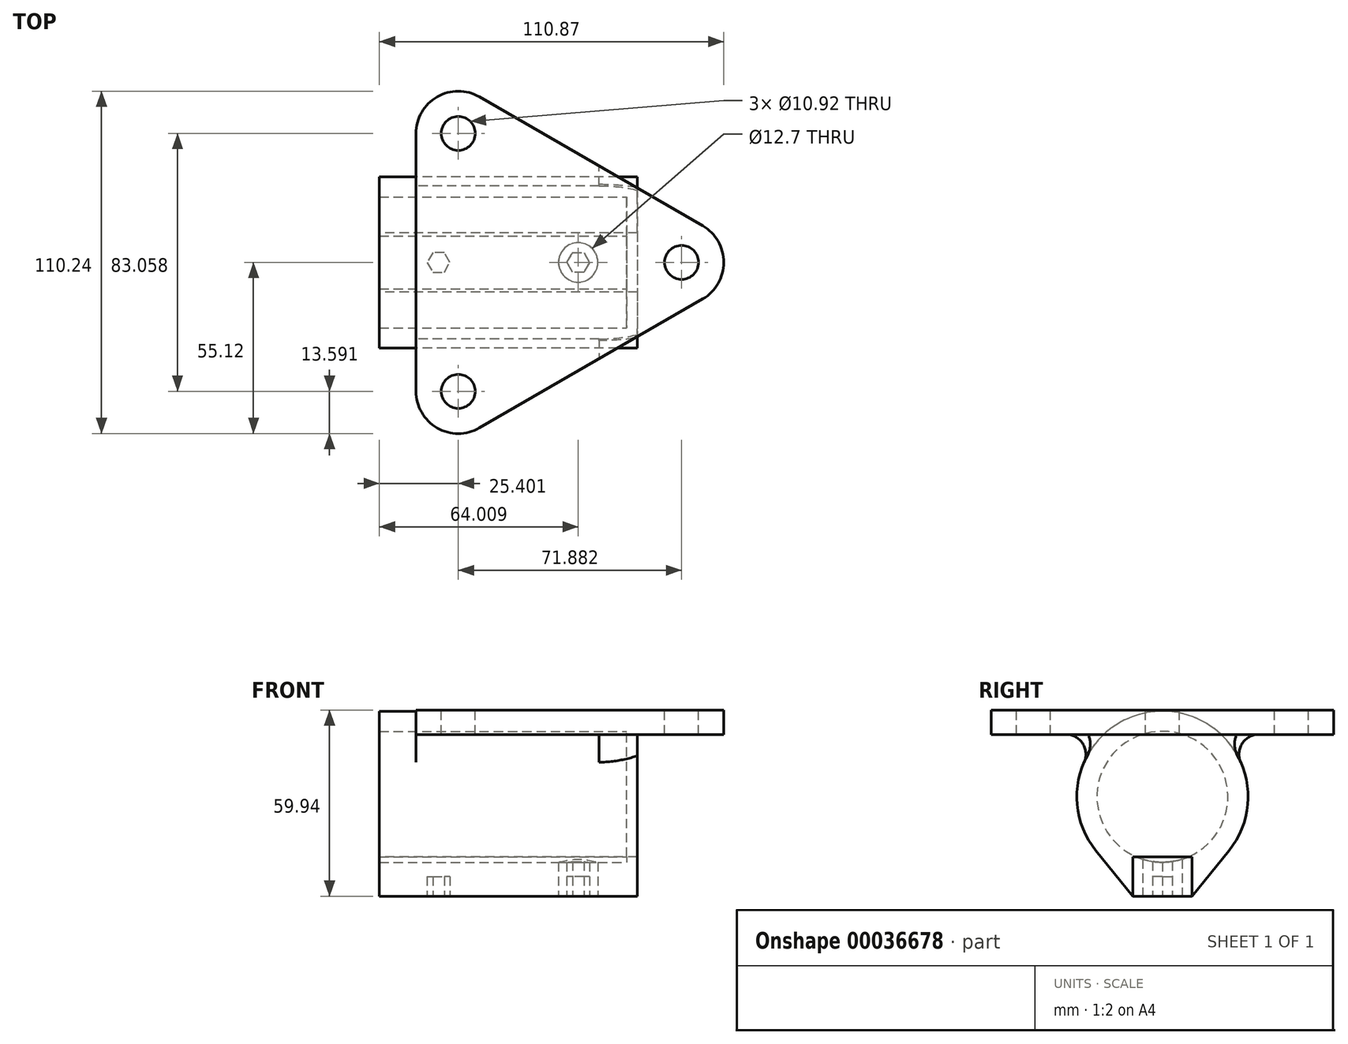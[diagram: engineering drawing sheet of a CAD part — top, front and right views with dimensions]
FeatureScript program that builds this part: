
annotation { "Feature Type Name" : "Feature", "Feature Type Description" : "" }
export const myFeature = defineFeature(function(context is Context, id is Id, definition is map)
    precondition{}
    {
        {
            var Q0;
            Q0=qCreatedBy(makeId("Right.planeOp"),FACE);
            var sketch = newSketch(context, id + "F0", { "sketchPlane" : qUnion([Q0])});
            skCircle(sketch, "E0", {"center": v(0, 0) * mm, "radius": 21.08 * mm});
            skCircle(sketch, "E1", {"center": v(0, 0) * mm, "radius": 27.56 * mm});
            skLineSegment(sketch, "E2.rect.top", {"start": v(9.53, -32) * mm, "end": v(-9.53, -32) * mm});
            skLineSegment(sketch, "E3", {"start": v(-9.52, -32) * mm, "end": v(-21.4, -17.36) * mm});
            skLineSegment(sketch, "E4", {"start": v(9.53, -32) * mm, "end": v(21.4, -17.36) * mm});
            skSolve(sketch);
        }
        {
            var Q0;
            Q0=makeQuery(id+"F0.imprint","IMPRINT",FACE,{"disambiguationData":[TD([[makeQuery(id+"F0.imprint","IMPRINT",EDGE,{"derivedFrom":sQuery(id+"F0.wireOp",EDGE,"E0")}),-1.0]])]});
            var Q1;
            Q1=makeQuery(id+"F0.imprint","IMPRINT",FACE,{"disambiguationData":[TD([[makeQuery(id+"F0.imprint","IMPRINT",EDGE,{"derivedFrom":sQuery(id+"F0.wireOp",EDGE,"E2.rect.top")}),-1.0]])]});
            var Q2;
            Q2=makeQuery(id+"F0.imprint","IMPRINT",FACE,{"disambiguationData":[TD([[makeQuery(id+"F0.imprint","IMPRINT",EDGE,{"derivedFrom":sQuery(id+"F0.wireOp",EDGE,"E0")}),1.0]])]});
            extrude(context, id + "F1", {"entities" : qUnion([Q0, Q1, Q2]), "endBound" : BoundingType.SYMMETRIC, "depth" : 83.06 * mm});
        }
        {
            var Q0;
            Q0=makeQuery(id+"F1.opExtrude","SWEPT_FACE",FACE,{"disambiguationData":[OSD([sQuery(id+"F0.wireOp",EDGE,"E2.rect.top")])]});
            var sketch = newSketch(context, id + "F2", { "sketchPlane" : qUnion([Q0])});
            skCircle(sketch, "E5", {"center": v(-22.48, 0) * mm, "radius": 6.35 * mm});
            skCircle(sketch, "E6.cCircle", {"center": v(-22.48, 0) * mm, "radius": 3.18 * mm, "construction": true});
            skLineSegment(sketch, "E6.0", {"start": v(-24.31, 3.18) * mm, "end": v(-20.65, 3.18) * mm});
            skLineSegment(sketch, "E6.1", {"start": v(-20.65, 3.17) * mm, "end": v(-18.81, 0) * mm});
            skLineSegment(sketch, "E6.2", {"start": v(-18.81, 0) * mm, "end": v(-20.65, -3.18) * mm});
            skLineSegment(sketch, "E6.3", {"start": v(-20.65, -3.17) * mm, "end": v(-24.31, -3.18) * mm});
            skLineSegment(sketch, "E6.4", {"start": v(-24.31, -3.18) * mm, "end": v(-26.15, 0) * mm});
            skLineSegment(sketch, "E6.5", {"start": v(-26.15, 0) * mm, "end": v(-24.31, 3.17) * mm});
            skPoint(sketch, "E6.0.midPoint", {"position": v(-22.48, 3.18) * mm});
            skCircle(sketch, "E7.MirrorC", {"center": v(22.48, 0) * mm, "radius": 6.35 * mm});
            skLineSegment(sketch, "E8.MirrorCS", {"start": v(24.31, 3.17) * mm, "end": v(20.65, 3.17) * mm});
            skLineSegment(sketch, "E9.MirrorCS", {"start": v(20.65, 3.18) * mm, "end": v(18.81, 0) * mm});
            skLineSegment(sketch, "E10.MirrorCS", {"start": v(18.81, 0) * mm, "end": v(20.65, -3.17) * mm});
            skLineSegment(sketch, "E11.MirrorCS", {"start": v(20.65, -3.17) * mm, "end": v(24.31, -3.17) * mm});
            skLineSegment(sketch, "E12.MirrorCS", {"start": v(24.31, -3.18) * mm, "end": v(26.15, 0) * mm});
            skLineSegment(sketch, "E13.MirrorCS", {"start": v(26.15, 0) * mm, "end": v(24.31, 3.17) * mm});
            skSolve(sketch);
        }
        {
            var Q0;
            Q0=makeQuery(id+"F2.imprint","IMPRINT",FACE,{"disambiguationData":[TD([[makeQuery(id+"F2.imprint","IMPRINT",EDGE,{"derivedFrom":sQuery(id+"F2.wireOp",EDGE,"E6.0")}),-1.0]])]});
            var Q1;
            Q1=makeQuery(id+"F2.imprint","IMPRINT",FACE,{"disambiguationData":[TD([[makeQuery(id+"F2.imprint","IMPRINT",EDGE,{"derivedFrom":sQuery(id+"F2.wireOp",EDGE,"E5")}),1.0]])]});
            var Q2;
            Q2=makeQuery(id+"F2.imprint","IMPRINT",FACE,{"disambiguationData":[TD([[makeQuery(id+"F2.imprint","IMPRINT",EDGE,{"derivedFrom":sQuery(id+"F2.wireOp",EDGE,"E8.MirrorCS")}),1.0]])]});
            var Q3;
            Q3=makeQuery(id+"F2.imprint","IMPRINT",FACE,{"disambiguationData":[TD([[makeQuery(id+"F2.imprint","IMPRINT",EDGE,{"derivedFrom":sQuery(id+"F2.wireOp",EDGE,"E7.MirrorC")}),-1.0]])]});
            extrude(context, id + "F3", {"entities" : qUnion([Q0, Q1, Q2, Q3]), "oppositeDirection" : true, "depth" : 12.7 * mm});
        }
        {
            var Q0;
            Q0=makeQuery(id+"F3.opExtrude","SWEPT_BODY",BODY,{"disambiguationData":[OSD([sQuery(id+"F2.wireOp",EDGE,"E5")])]});
            var Q1;
            Q1=makeQuery(id+"F3.opExtrude","SWEPT_BODY",BODY,{"disambiguationData":[OSD([sQuery(id+"F2.wireOp",EDGE,"E7.MirrorC")])]});
            var Q2;
            Q2=makeQuery(id+"FDmkU0JhcyfajZN_1.opExtrude","SWEPT_BODY",BODY,{"disambiguationData":[OSD([sQuery(id+"Fau4lb0L3iw3XX0_1.wireOp",EDGE,"aa76d7ee-a35b-4488-8276-169a7f60b04d")])]});
            var Q3;
            Q3=makeQuery(id+"F1.opExtrude","SWEPT_BODY",BODY,{"disambiguationData":[OSD([sQuery(id+"F0.wireOp",EDGE,"E1"),sQuery(id+"F0.wireOp",EDGE,"E2.rect.bottom"),sQuery(id+"F0.wireOp",EDGE,"E2.rect.top"),sQuery(id+"F0.wireOp",EDGE,"a51bb4f6-294f-47ed-b473-a52ab50b22ea"),sQuery(id+"F0.wireOp",EDGE,"8497208a-9e24-4526-a7f4-8772f674d511"),sQuery(id+"F0.wireOp",EDGE,"E3"),sQuery(id+"F0.wireOp",EDGE,"E4")])]});
            booleanBodies(context, id + "F4", {"operationType" : BooleanOperationType.SUBTRACTION, "tools" : qUnion([Q0, Q1, Q2]), "targets" : qUnion([Q3]), "keepTools" : true});
        }
        {
            var Q0;
            Q0=makeQuery(id+"F2.imprint","IMPRINT",FACE,{"disambiguationData":[TD([[makeQuery(id+"F2.imprint","IMPRINT",EDGE,{"derivedFrom":sQuery(id+"F2.wireOp",EDGE,"E6.0")}),-1.0]])]});
            var Q1;
            Q1=makeQuery(id+"F2.imprint","IMPRINT",FACE,{"disambiguationData":[TD([[makeQuery(id+"F2.imprint","IMPRINT",EDGE,{"derivedFrom":sQuery(id+"F2.wireOp",EDGE,"E8.MirrorCS")}),1.0]])]});
            extrude(context, id + "F5", {"entities" : qUnion([Q0, Q1]), "operationType" : NewBodyOperationType.REMOVE, "oppositeDirection" : true, "depth" : 6.35 * mm});
        }
        {
            var Q0;
            Q0=qCreatedBy(makeId("Top.planeOp"),FACE);
            cPlane(context, id + "F6", {"entities" : qUnion([Q0]), "cplaneType" : CPlaneType.OFFSET, "offset" : 27.94 * mm, "width" : 152.4 * mm, "height" : 152.4 * mm});
        }
        {
            var Q0;
            Q0=qCreatedBy(id+"F6.planeOp",FACE);
            var sketch = newSketch(context, id + "F7", { "sketchPlane" : qUnion([Q0])});
            skLineSegment(sketch, "E14", {"start": v(55.75, 0) * mm, "end": v(-16.13, -41.53) * mm, "construction": true});
            skLineSegment(sketch, "E15", {"start": v(-16.13, -41.53) * mm, "end": v(-16.13, 41.53) * mm, "construction": true});
            skLineSegment(sketch, "E16", {"start": v(-16.13, 41.53) * mm, "end": v(55.75, 0) * mm, "construction": true});
            skCircle(sketch, "E17", {"center": v(-16.13, 41.53) * mm, "radius": 5.46 * mm});
            skCircle(sketch, "E18", {"center": v(-16.13, -41.53) * mm, "radius": 5.46 * mm});
            skCircle(sketch, "E19", {"center": v(55.75, 0) * mm, "radius": 5.46 * mm});
            skCircle(sketch, "E20", {"center": v(55.75, 0) * mm, "radius": 13.59 * mm});
            skCircle(sketch, "E21", {"center": v(-16.13, -41.53) * mm, "radius": 13.59 * mm});
            skCircle(sketch, "E22", {"center": v(-16.13, 41.53) * mm, "radius": 13.59 * mm});
            skLineSegment(sketch, "E23", {"start": v(-9.33, 53.3) * mm, "end": v(62.55, 11.77) * mm});
            skLineSegment(sketch, "E24", {"start": v(-29.72, 41.53) * mm, "end": v(-29.72, -41.53) * mm});
            skLineSegment(sketch, "E25", {"start": v(-9.33, -53.3) * mm, "end": v(62.55, -11.77) * mm});
            skSolve(sketch);
        }
        {
            var Q0;
            {var subQ2=sQuery(id+"F7.wireOp",EDGE,"E23");Q0=makeQuery(id+"F7.imprint","IMPRINT",FACE,{"disambiguationData":[TD([[makeQuery(id+"F7.imprint","IMPRINT",EDGE,{"derivedFrom":subQ2}),-1.0]])]});}
            var Q1;
            Q1=makeQuery(id+"F7.imprint","IMPRINT",FACE,{"disambiguationData":[TD([[makeQuery(id+"F7.imprint","IMPRINT",EDGE,{"derivedFrom":sQuery(id+"F7.wireOp",EDGE,"E17")}),-1.0]])]});
            var Q2;
            Q2=makeQuery(id+"F7.imprint","IMPRINT",FACE,{"disambiguationData":[TD([[makeQuery(id+"F7.imprint","IMPRINT",EDGE,{"derivedFrom":sQuery(id+"F7.wireOp",EDGE,"E18")}),-1.0]])]});
            var Q3;
            Q3=makeQuery(id+"F7.imprint","IMPRINT",FACE,{"disambiguationData":[TD([[makeQuery(id+"F7.imprint","IMPRINT",EDGE,{"derivedFrom":sQuery(id+"F7.wireOp",EDGE,"E19")}),-1.0]])]});
            extrude(context, id + "F8", {"entities" : qUnion([Q0, Q1, Q2, Q3]), "operationType" : NewBodyOperationType.ADD, "oppositeDirection" : true, "depth" : 7.87 * mm});
        }
        {
            var Q0;
            Q0=makeQuery(id+"F0.imprint","IMPRINT",FACE,{"disambiguationData":[TD([[makeQuery(id+"F0.imprint","IMPRINT",EDGE,{"derivedFrom":sQuery(id+"F0.wireOp",EDGE,"E0")}),1.0]])]});
            extrude(context, id + "F9", {"entities" : qUnion([Q0]), "operationType" : NewBodyOperationType.REMOVE, "endBound" : BoundingType.THROUGH_ALL, "oppositeDirection" : true, "depth" : 25.4 * mm, "hasSecondDirection" : true, "secondDirectionOppositeDirection" : false, "secondDirectionDepth" : 38.1 * mm});
        }
        {
            var Q0;
            Q0=makeQuery(id+"F8.boolean.opBoolean","INTERSECT",EDGE,{"disambiguationData":[OD(1.0)],"derivedFrom":[makeQuery(id+"F1.opExtrude","SWEPT_FACE",FACE,{"disambiguationData":[OSD([sQuery(id+"F0.wireOp",EDGE,"E1")])]}),makeQuery(id+"F8.opExtrude","CAP_FACE",FACE,{"disambiguationData":[OSD([sQuery(id+"F7.wireOp",EDGE,"E17"),sQuery(id+"F7.wireOp",EDGE,"E18"),sQuery(id+"F7.wireOp",EDGE,"E19"),sQuery(id+"F7.wireOp",EDGE,"E20"),sQuery(id+"F7.wireOp",EDGE,"E21"),sQuery(id+"F7.wireOp",EDGE,"E22"),sQuery(id+"F7.wireOp",EDGE,"E23"),sQuery(id+"F7.wireOp",EDGE,"E24"),sQuery(id+"F7.wireOp",EDGE,"E25")])],"isStart":false})]});
            var Q1;
            Q1=makeQuery(id+"F8.boolean.opBoolean","INTERSECT",EDGE,{"disambiguationData":[OD(0.0)],"derivedFrom":[makeQuery(id+"F1.opExtrude","SWEPT_FACE",FACE,{"disambiguationData":[OSD([sQuery(id+"F0.wireOp",EDGE,"E1")])]}),makeQuery(id+"F8.opExtrude","CAP_FACE",FACE,{"disambiguationData":[OSD([sQuery(id+"F7.wireOp",EDGE,"E17"),sQuery(id+"F7.wireOp",EDGE,"E18"),sQuery(id+"F7.wireOp",EDGE,"E19"),sQuery(id+"F7.wireOp",EDGE,"E20"),sQuery(id+"F7.wireOp",EDGE,"E21"),sQuery(id+"F7.wireOp",EDGE,"E22"),sQuery(id+"F7.wireOp",EDGE,"E23"),sQuery(id+"F7.wireOp",EDGE,"E24"),sQuery(id+"F7.wireOp",EDGE,"E25")])],"isStart":false})]});
            fillet(context, id + "F10", {"entities" : qUnion([Q0, Q1]), "radius" : 6.35 * mm, "tangentPropagation" : true, "allowEdgeOverflow" : false});
        }
    });
